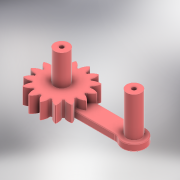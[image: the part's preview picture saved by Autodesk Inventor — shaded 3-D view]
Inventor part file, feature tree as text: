
AUTODESK INVENTOR PART (.ipt)
format: ipt  version: 2021 (Build 250183000, 183)  size: 1,332,736 bytes
history: native  units: mm
features: sketch x5, extrude x4, other x1, fillet x1, hole x1
ambient origin geometry x8: Origin, YZ Plane, XZ Plane, XY Plane, X Axis, Y Axis, Z Axis, Center Point
bodies: Body1 (feature_tree)
feature tree (12):
  other  "Sólido1"
  extrude  "Extrusão2"  Depth=17.0mm
  fillet  "Arredondamento2"  Radius=19.266667mm
  extrude  "Extrusão1"  Depth=14.733333mm
  extrude  "Extrusão3"  Depth=1.047198mm
  hole  "Furo1"  [1 undecoded]
  extrude  "Extrusão4"  Depth=3.0mm
  sketch  "Esboço1"  dims[d7=5.5mm d8=0.0mm d13=17.0mm d23=19.266667mm]
  sketch  "Esboço2"  dims[d24=1.133333mm d25=14.733333mm]
  sketch  "Esboço3"  dims[d45=1.047198mm d46=1.047198mm d47=1.047198mm]
  sketch  "Esboço4"  dims[d48=1.047198mm d49=1.047198mm]
  sketch  "Esboço5"  dims[d51=1.047198mm d52=1.047198mm d53=1.047198mm d54=1.047198mm d56=0.188889mm d57=1.047198mm d64=6.0mm d65=3.0mm d67=15.0mm d68=0.0mm d69=15.0mm d70=8.0mm d71=7.0mm d73=1.047198mm d74=1.047198mm d83=150.0mm d85=360.0deg d87=150.0mm d89=360.0deg d91=2.5mm d92=0.0mm d93=0.3mm d94=25.0mm d95=4.0mm d97=5.0mm d98=13.7mm d99=0.0mm d100=1.5mm d101=6.0mm d102=4.0mm d103=2.0mm d104=90.0deg d105=10.0mm d106=20.594885mm d109=14.835299mm d111=0.1mm d113=5.4mm d115=2.3mm d116=200.0mm d118=360.0deg d120=3.0mm d121=0.0mm]
note: 1 required parameter value undecoded (feature->parameter linkage not recoverable at this tier; creation-order binding heuristic only, values carry confidence <= 0.55)
